# Revit family: FU_Chair_Sandler_Hellen One SE02
name_source: partatom
category: Furniture
units: mm (PartAtom-declared; Revit-internal decimal feet)

## family parameters
Always vertical = Yes
Cut with Voids When Loaded = No
OmniClass Number = 23.40.20.00
OmniClass Title = General Furniture and Specialties
Room Calculation Point = No
Shared = No
Work Plane-Based = No

## types (1)
- Hellen One SE02
    Default Elevation = 0 mm  [stored 0 ft]
    Depth = 500 mm  [stored 1.64042 ft]
    Description = Chair with upholstered seat on a solid beech wood frame. Stackable up to five chairs.
    Frame = Wood - Beech - Walnut - V
    Height = 825 mm  [stored 2.70669 ft]
    Manufacturer = Sandler
    Model = Hellen One SE02
    URL = https://www.sandlerseating.com
    Upholstery = Leather - White - Sandler 117
    Width = 500 mm  [stored 1.64042 ft]

note: [stored X ft] marks values corroborated as IEEE doubles in the binary element streams (Revit-internal decimal feet)

## geometry (parser evidence)
native form markers: Sweep x9
no freeform markers — native parametric forms only
